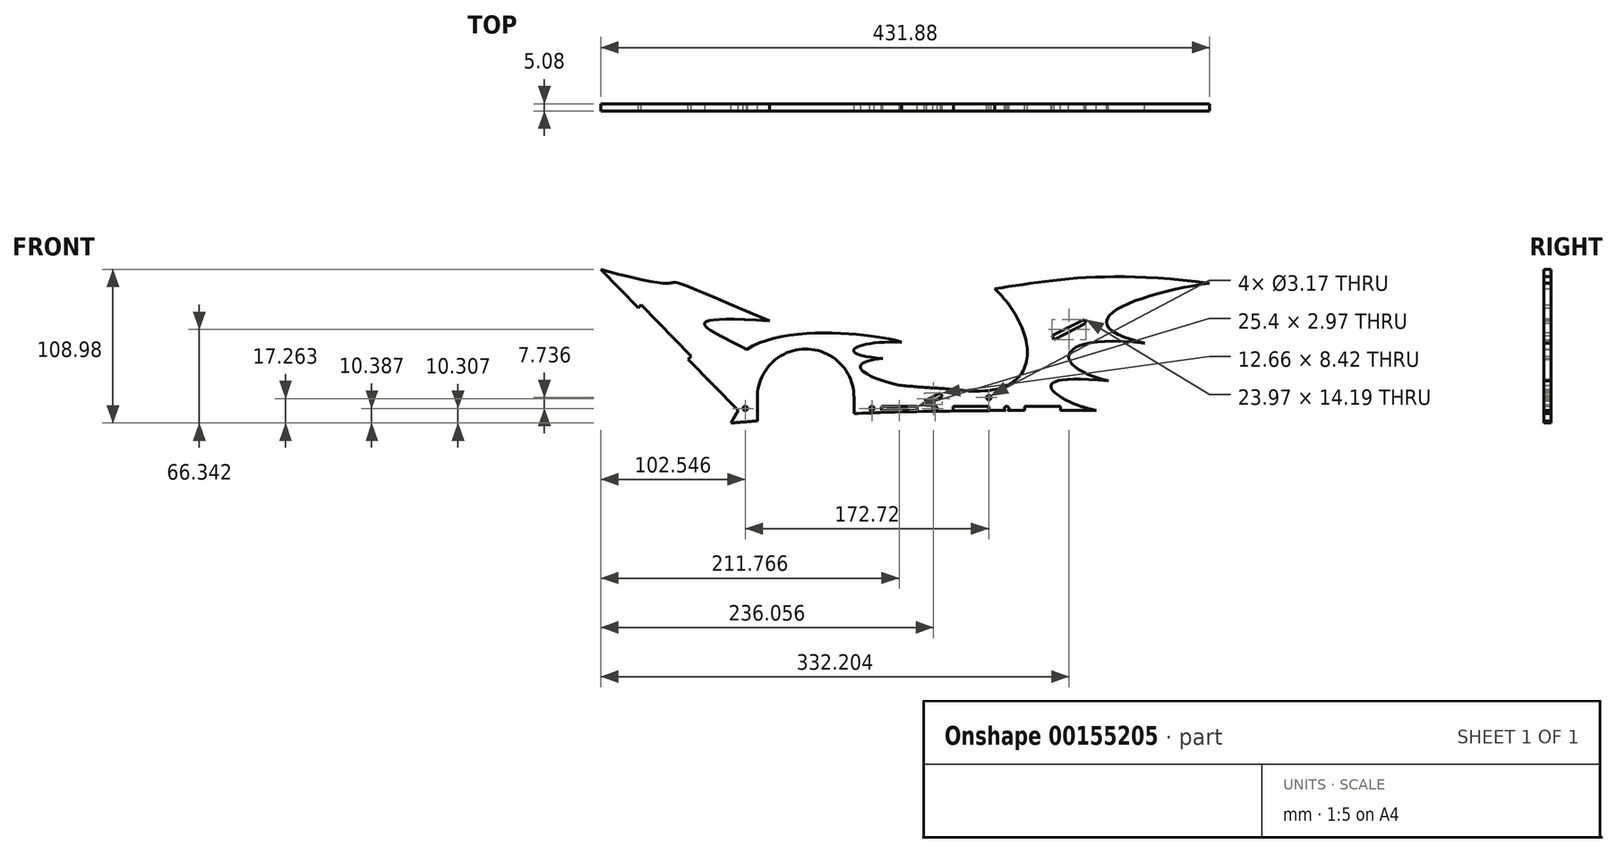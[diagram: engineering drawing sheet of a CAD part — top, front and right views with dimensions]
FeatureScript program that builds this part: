
annotation { "Feature Type Name" : "Feature", "Feature Type Description" : "" }
export const myFeature = defineFeature(function(context is Context, id is Id, definition is map)
    precondition{}
    {
        {
            var Q0;
            Q0=qCreatedBy(makeId("Front.planeOp"),FACE);
            var sketch = newSketch(context, id + "F0", { "sketchPlane" : qUnion([Q0])});
            skLineSegment(sketch, "E0", {"start": v(-123.58, -55.43) * mm, "end": v(130.42, -55.43) * mm});
            skLineSegment(sketch, "E1", {"start": v(-123.58, -55.43) * mm, "end": v(-221.05, 44.65) * mm});
            skFitSpline(sketch, "E2", {"points": [v(-221.05, 44.65) * mm, v(130.42, -55.43) * mm], "startDerivative": vector(505.8, -343.12) * mm, "endDerivative": vector(351.47, -100.08) * mm});
            skFitSpline(sketch, "E3", {"points": [v(-128.49, -64.33) * mm, v(130.42, -55.43) * mm], "startDerivative": vector(268.45, 20.89) * mm, "endDerivative": vector(540.39, 0) * mm});
            skFitSpline(sketch, "E4", {"points": [v(130.42, -55.43) * mm, v(139.17, -34.48) * mm], "startDerivative": vector(-76.13, 14.57) * mm, "endDerivative": vector(210.33, -21.7) * mm});
            skFitSpline(sketch, "E5", {"points": [v(139.17, -34.48) * mm, v(164.77, -7.78) * mm], "startDerivative": vector(-128.53, 30.04) * mm, "endDerivative": vector(193.64, -23.33) * mm});
            skFitSpline(sketch, "E6", {"points": [v(164.77, -7.78) * mm, v(210.83, 34.92) * mm], "startDerivative": vector(-195.3, 48.4) * mm, "endDerivative": vector(131.87, 18.36) * mm});
            skFitSpline(sketch, "E7", {"points": [v(58.39, 30.96) * mm, v(29.04, -40.35) * mm], "startDerivative": vector(97.12, -92.88) * mm, "endDerivative": vector(-201.85, 31.32) * mm});
            skLineSegment(sketch, "E8", {"start": v(-128.49, -64.33) * mm, "end": v(-123.58, -55.43) * mm});
            skLineSegment(sketch, "E9.bottom", {"start": v(-123.58, -55.43) * mm, "end": v(-97.17, -55.43) * mm});
            skLineSegment(sketch, "E9.right", {"start": v(-97.17, -55.43) * mm, "end": v(-97.17, -52.46) * mm});
            skCircle(sketch, "E10", {"center": v(-75.7, -46.1) * mm, "radius": 34.3 * mm});
            skFitSpline(sketch, "E11", {"points": [v(-117.55, -12.17) * mm, v(-7.73, -7.1) * mm], "startDerivative": vector(92.66, 61.07) * mm, "endDerivative": vector(22.09, -10.97) * mm});
            skFitSpline(sketch, "E12", {"points": [v(-7.73, -7.1) * mm, v(-21.01, -18.44) * mm], "startDerivative": vector(-102.02, 5.3) * mm, "endDerivative": vector(107.38, -6.32) * mm});
            skFitSpline(sketch, "E13", {"points": [v(-21.01, -18.44) * mm, v(-9.26, -37.58) * mm], "startDerivative": vector(-79.92, -7.05) * mm, "endDerivative": vector(88.35, -20.41) * mm});
            skLineSegment(sketch, "E14", {"start": v(-41.41, -45.74) * mm, "end": v(-41.41, -57.67) * mm});
            skLineSegment(sketch, "E15", {"start": v(-109.98, -47.01) * mm, "end": v(-109.98, -62.85) * mm});
            skLineSegment(sketch, "E16.bottom", {"start": v(105.02, -55.44) * mm, "end": v(79.62, -55.44) * mm});
            skLineSegment(sketch, "E16.top", {"start": v(105.02, -52.47) * mm, "end": v(79.62, -52.47) * mm});
            skLineSegment(sketch, "E16.left", {"start": v(105.02, -55.44) * mm, "end": v(105.02, -52.47) * mm});
            skLineSegment(sketch, "E16.right", {"start": v(79.62, -55.44) * mm, "end": v(79.62, -52.47) * mm});
            skLineSegment(sketch, "E17.bottom", {"start": v(54.22, -55.6) * mm, "end": v(28.82, -55.6) * mm});
            skLineSegment(sketch, "E17.top", {"start": v(54.22, -52.64) * mm, "end": v(28.82, -52.64) * mm});
            skLineSegment(sketch, "E17.left", {"start": v(54.22, -55.6) * mm, "end": v(54.22, -52.64) * mm});
            skLineSegment(sketch, "E17.right", {"start": v(28.82, -55.6) * mm, "end": v(28.82, -52.64) * mm});
            skLineSegment(sketch, "E18.bottom", {"start": v(3.42, -55.43) * mm, "end": v(-21.98, -55.43) * mm});
            skLineSegment(sketch, "E18.top", {"start": v(3.42, -52.46) * mm, "end": v(-21.98, -52.46) * mm});
            skLineSegment(sketch, "E18.left", {"start": v(3.42, -55.43) * mm, "end": v(3.42, -52.46) * mm});
            skLineSegment(sketch, "E18.right", {"start": v(-21.98, -55.43) * mm, "end": v(-21.98, -52.46) * mm});
            skFitSpline(sketch, "E19", {"points": [v(58.39, 30.96) * mm, v(210.83, 34.92) * mm], "startDerivative": vector(114.82, 16.8) * mm, "endDerivative": vector(230.04, -29.22) * mm});
            skCircle(sketch, "E20", {"center": v(-75.7, -46.1) * mm, "radius": 1.59 * mm});
            skPoint(sketch, "E21.centerSnap0", {"position": v(41.52, -52.64) * mm});
            skPoint(sketch, "E22.centerSnap0", {"position": v(92.32, -55.44) * mm});
            skLineSegment(sketch, "E23", {"start": v(-159.03, -19.04) * mm, "end": v(-156.9, -16.96) * mm});
            skLineSegment(sketch, "E24", {"start": v(-156.9, -16.96) * mm, "end": v(-192.34, 19.43) * mm});
            skLineSegment(sketch, "E25", {"start": v(-192.34, 19.43) * mm, "end": v(-194.47, 17.36) * mm});
            skFitSpline(sketch, "E26", {"points": [v(-221.05, 44.65) * mm, v(-101.36, 8.06) * mm], "startDerivative": vector(291.26, -78.7) * mm, "endDerivative": vector(356.14, -152.13) * mm});
            skFitSpline(sketch, "E27", {"points": [v(-101.36, 8.06) * mm, v(-117.55, -12.17) * mm], "startDerivative": vector(-235.62, 17) * mm, "endDerivative": vector(64.38, -36.5) * mm});
            skCircle(sketch, "E28", {"center": v(-118.5, -54.02) * mm, "radius": 1.59 * mm});
            skCircle(sketch, "E29", {"center": v(-28.65, -54.02) * mm, "radius": 1.59 * mm});
            skCircle(sketch, "E30", {"center": v(66.92, -54.02) * mm, "radius": 1.59 * mm});
            skCircle(sketch, "E31", {"center": v(16.12, -54.02) * mm, "radius": 1.59 * mm});
            skCircle(sketch, "E32", {"center": v(54.22, -46.29) * mm, "radius": 1.59 * mm});
            skLineSegment(sketch, "E33", {"start": v(8.67, -48.63) * mm, "end": v(19.99, -42.86) * mm});
            skLineSegment(sketch, "E34", {"start": v(8.67, -48.63) * mm, "end": v(10.03, -51.28) * mm});
            skLineSegment(sketch, "E35", {"start": v(19.99, -42.86) * mm, "end": v(21.34, -45.5) * mm});
            skLineSegment(sketch, "E36", {"start": v(10.03, -51.28) * mm, "end": v(21.34, -45.5) * mm});
            skLineSegment(sketch, "E37", {"start": v(8.67, -48.63) * mm, "end": v(121.8, 9.1) * mm});
            skLineSegment(sketch, "E38", {"start": v(10.03, -51.28) * mm, "end": v(123.14, 6.46) * mm});
            skLineSegment(sketch, "E39", {"start": v(121.8, 9.1) * mm, "end": v(123.14, 6.46) * mm});
            skLineSegment(sketch, "E40", {"start": v(99.17, -2.44) * mm, "end": v(100.52, -5.09) * mm});
            skSolve(sketch);
        }
        {
            var Q0;
            {var subQ4=sQuery(id+"F0.wireOp",EDGE,"E1");Q0=makeQuery(id+"F0.imprint","IMPRINT",FACE,{"disambiguationData":[TD([[makeQuery(id+"F0.imprint","IMPRINT",EDGE,{"derivedFrom":subQ4}),-1.0]])]});}
            var Q1;
            {var subQ5=sQuery(id+"F0.wireOp",EDGE,"E11");Q1=makeQuery(id+"F0.imprint","IMPRINT",FACE,{"disambiguationData":[TD([[makeQuery(id+"F0.imprint","IMPRINT",EDGE,{"derivedFrom":subQ5}),-1.0]])]});}
            var Q2;
            {var subQ2=sQuery(id+"F0.wireOp",EDGE,"E17.top");Q2=makeQuery(id+"F0.imprint","IMPRINT",FACE,{"disambiguationData":[TD([[makeQuery(id+"F0.imprint","IMPRINT",EDGE,{"derivedFrom":subQ2}),-1.0]])]});}
            var Q3;
            {var subQ6=sQuery(id+"F0.wireOp",EDGE,"E8");Q3=makeQuery(id+"F0.imprint","IMPRINT",FACE,{"disambiguationData":[TD([[makeQuery(id+"F0.imprint","IMPRINT",EDGE,{"derivedFrom":subQ6}),-1.0]])]});}
            var Q4;
            {var subQ0=sQuery(id+"F0.wireOp",EDGE,"E5");Q4=makeQuery(id+"F0.imprint","IMPRINT",FACE,{"disambiguationData":[TD([[makeQuery(id+"F0.imprint","IMPRINT",EDGE,{"derivedFrom":subQ0}),1.0]])]});}
            var Q5;
            {var subQ0=sQuery(id+"F0.wireOp",EDGE,"E9.left");Q5=makeQuery(id+"F0.imprint","IMPRINT",FACE,{"disambiguationData":[TD([[makeQuery(id+"F0.imprint","IMPRINT",EDGE,{"derivedFrom":subQ0}),-1.0]])]});}
            var Q6;
            {var subQ0=sQuery(id+"F0.wireOp",EDGE,"kmsJGGKl-0SAu-e9FC-bgvf-i3T3cF3yvVrz");var subQ1=sQuery(id+"F0.wireOp",EDGE,"E9.bottom");var subQ2=makeQuery(id+"F0.imprint","INTERSECT",VERTEX,{"disambiguationData":[OD(1.0)],"derivedFrom":[subQ1,subQ0]});Q6=makeQuery(id+"F0.imprint","IMPRINT",FACE,{"disambiguationData":[TD([[makeQuery(id+"F0.imprint","IMPRINT",EDGE,{"disambiguationData":[TD([[subQ2,-1.0]])],"derivedFrom":subQ1}),1.0]])]});}
            var Q7;
            {var subQ0=sQuery(id+"F0.wireOp",EDGE,"E26");Q7=makeQuery(id+"F0.imprint","IMPRINT",FACE,{"disambiguationData":[TD([[makeQuery(id+"F0.imprint","IMPRINT",EDGE,{"derivedFrom":subQ0}),-1.0]])]});}
            var Q8;
            {var subQ1=sQuery(id+"F0.wireOp",EDGE,"E17.bottom");Q8=makeQuery(id+"F0.imprint","IMPRINT",FACE,{"disambiguationData":[TD([[makeQuery(id+"F0.imprint","IMPRINT",EDGE,{"derivedFrom":subQ1}),1.0]])]});}
            var Q9;
            {var subQ5=sQuery(id+"F0.wireOp",EDGE,"E40");Q9=makeQuery(id+"F0.imprint","IMPRINT",FACE,{"disambiguationData":[TD([[makeQuery(id+"F0.imprint","IMPRINT",EDGE,{"derivedFrom":subQ5}),-1.0]])]});}
            var Q10;
            {var subQ1=sQuery(id+"F0.wireOp",EDGE,"E35");Q10=makeQuery(id+"F0.imprint","IMPRINT",FACE,{"disambiguationData":[TD([[makeQuery(id+"F0.imprint","IMPRINT",EDGE,{"derivedFrom":subQ1}),1.0]])]});}
            extrude(context, id + "F1", {"entities" : qUnion([Q0, Q1, Q2, Q3, Q4, Q5, Q6, Q7, Q8, Q9, Q10]), "depth" : 2.54 * mm});
        }
        {
            var Q0;
            Q0=makeQuery(id+"F1.opExtrude","CAP_FACE",FACE,{"disambiguationData":[OSD([sQuery(id+"F0.wireOp",EDGE,"E0"),sQuery(id+"F0.wireOp",EDGE,"E1"),sQuery(id+"F0.wireOp",EDGE,"E2"),sQuery(id+"F0.wireOp",EDGE,"E3"),sQuery(id+"F0.wireOp",EDGE,"E4"),sQuery(id+"F0.wireOp",EDGE,"E5"),sQuery(id+"F0.wireOp",EDGE,"E6"),sQuery(id+"F0.wireOp",EDGE,"E7"),sQuery(id+"F0.wireOp",EDGE,"E8"),sQuery(id+"F0.wireOp",EDGE,"E9.bottom"),sQuery(id+"F0.wireOp",EDGE,"E10"),sQuery(id+"F0.wireOp",EDGE,"E11"),sQuery(id+"F0.wireOp",EDGE,"E12"),sQuery(id+"F0.wireOp",EDGE,"E13"),sQuery(id+"F0.wireOp",EDGE,"E14"),sQuery(id+"F0.wireOp",EDGE,"E15"),sQuery(id+"F0.wireOp",EDGE,"E16.top"),sQuery(id+"F0.wireOp",EDGE,"E16.left"),sQuery(id+"F0.wireOp",EDGE,"E16.right"),sQuery(id+"F0.wireOp",EDGE,"E17.top"),sQuery(id+"F0.wireOp",EDGE,"E17.left"),sQuery(id+"F0.wireOp",EDGE,"E17.right"),sQuery(id+"F0.wireOp",EDGE,"E18.top"),sQuery(id+"F0.wireOp",EDGE,"E18.left"),sQuery(id+"F0.wireOp",EDGE,"E18.right"),sQuery(id+"F0.wireOp",EDGE,"E19"),sQuery(id+"F0.wireOp",EDGE,"HCBmPzbX-FsAB-Wz6B-1bXd-dk0utC5s3M7Y"),sQuery(id+"F0.wireOp",EDGE,"2KH3kkC5-nWMU-1kYx-wfHD-enwgcBDh3r1P"),sQuery(id+"F0.wireOp",EDGE,"E22")])],"isStart":false});
            var Q1;
            Q1=makeQuery(id+"F1.opExtrude","CAP_FACE",FACE,{"disambiguationData":[OSD([sQuery(id+"F0.wireOp",EDGE,"E0"),sQuery(id+"F0.wireOp",EDGE,"E1"),sQuery(id+"F0.wireOp",EDGE,"E2"),sQuery(id+"F0.wireOp",EDGE,"E3"),sQuery(id+"F0.wireOp",EDGE,"E4"),sQuery(id+"F0.wireOp",EDGE,"E5"),sQuery(id+"F0.wireOp",EDGE,"E6"),sQuery(id+"F0.wireOp",EDGE,"E7"),sQuery(id+"F0.wireOp",EDGE,"E8"),sQuery(id+"F0.wireOp",EDGE,"E9.bottom"),sQuery(id+"F0.wireOp",EDGE,"E10"),sQuery(id+"F0.wireOp",EDGE,"E11"),sQuery(id+"F0.wireOp",EDGE,"E12"),sQuery(id+"F0.wireOp",EDGE,"E13"),sQuery(id+"F0.wireOp",EDGE,"E14"),sQuery(id+"F0.wireOp",EDGE,"E15"),sQuery(id+"F0.wireOp",EDGE,"E16.top"),sQuery(id+"F0.wireOp",EDGE,"E16.left"),sQuery(id+"F0.wireOp",EDGE,"E16.right"),sQuery(id+"F0.wireOp",EDGE,"E17.top"),sQuery(id+"F0.wireOp",EDGE,"E17.left"),sQuery(id+"F0.wireOp",EDGE,"E17.right"),sQuery(id+"F0.wireOp",EDGE,"E18.top"),sQuery(id+"F0.wireOp",EDGE,"E18.left"),sQuery(id+"F0.wireOp",EDGE,"E18.right"),sQuery(id+"F0.wireOp",EDGE,"E19"),sQuery(id+"F0.wireOp",EDGE,"HCBmPzbX-FsAB-Wz6B-1bXd-dk0utC5s3M7Y"),sQuery(id+"F0.wireOp",EDGE,"2KH3kkC5-nWMU-1kYx-wfHD-enwgcBDh3r1P"),sQuery(id+"F0.wireOp",EDGE,"E22")])],"isStart":true});
            extrude(context, id + "F2", {"entities" : qUnion([Q0, Q1]), "operationType" : NewBodyOperationType.ADD, "depth" : 2.54 * mm});
        }
    });
